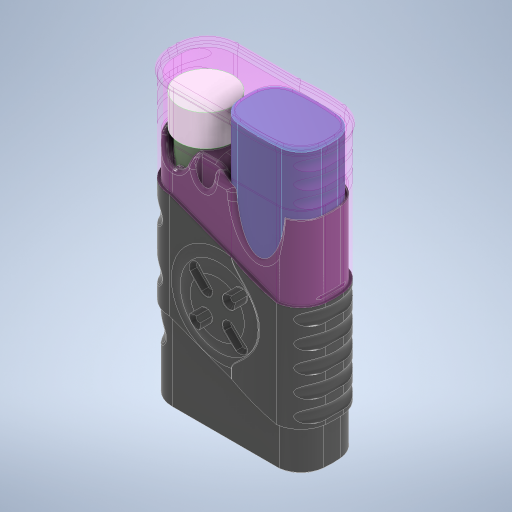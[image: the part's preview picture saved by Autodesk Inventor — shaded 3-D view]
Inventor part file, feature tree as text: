
AUTODESK INVENTOR PART (.ipt)
format: ipt  version: 2024.1 (Build 281209000, 209)  size: 4,207,616 bytes
history: native  units: mm
features: fillet x36, projected_geometry x32, extrude x28, sketch x14, other x6, revolve x6, sweep x2, pattern_circular x2, chamfer x2, plane x1, mirror x1
ambient origin geometry x8: Origin, YZ Plane, XZ Plane, XY Plane, X Axis, Y Axis, Z Axis, Center Point
bodies: Body1 (feature_tree), Body2 (feature_tree), Body3 (feature_tree), Body4 (feature_tree)
feature tree (130):
  other  "vape"
  extrude  "Extrusion1"  Depth=8.35mm
  fillet  "Fillet1"  Radius=80.0mm
  extrude  "Extrusion2"  Depth=11.6mm TaperAngle=0.0deg
  plane  "Work Plane1"
  extrude  "Extrusion3"  Depth=45.8mm TaperAngle=0.0deg
  extrude  "Extrusion4"  Depth=22.1mm
  extrude  "Extrusion5"  Depth=1.5mm
  extrude  "Extrusion6"  Depth=1.5mm
  fillet  "Fillet2"  Radius=1.5mm
  extrude  "Extrusion8"  Depth=15.55mm
  extrude  "Extrusion20"  Depth=3.0mm
  extrude  "Extrusion21"  Depth=3.0mm
  sweep  "Sweep2"
  extrude  "Extrusion22"  Depth=13.0mm
  fillet  "Fillet22"  Radius=2.0mm
  fillet  "Fillet23"  Radius=10.0mm
  fillet  "Fillet24"  Radius=11.0mm
  fillet  "Fillet25"  Radius=4.0mm
  fillet  "Fillet26"  Radius=2.0mm
  fillet  "Fillet4"  Radius=3.0mm
  extrude  "Extrusion10"  Depth=2.4mm
  extrude  "Extrusion11"  Depth=7.3mm
  fillet  "Fillet10"  Radius=7.0mm
  fillet  "Fillet27"  Radius=45.0mm
  extrude  "Extrusion13"  Depth=0.25mm
  fillet  "Fillet28"  Radius=71.0mm
  extrude  "Extrusion14"  Depth=71.0mm TaperAngle=0.0deg
  extrude  "Extrusion23"  Depth=3.0mm TaperAngle=30.0deg
  extrude  "Extrusion24"  Depth=1.0mm
  extrude  "Extrusion15"  Depth=15.0mm TaperAngle=0.0deg
  fillet  "Fillet29"  Radius=15.0mm
  extrude  "Extrusion25"  TaperAngle=0.0deg  [1 undecoded]
  fillet  "Fillet30"  [1 undecoded]
  other  "Work Axis1"
  sketch  "Sketch29"  dims[d28=17.0mm d29=45.8mm d30=0.0mm]
  revolve  "Revolution1"  [1 undecoded]
  sketch  "Sketch30"  dims[d31=17.0mm d38=22.1mm]
  revolve  "Revolution2"  [1 undecoded]
  fillet  "Fillet32"  Radius=20.0mm
  extrude  "Extrusion26"  Depth=9.0mm
  revolve  "Revolution3"  [1 undecoded]
  revolve  "Revolution5"  [1 undecoded]
  extrude  "Extrusion27"  Depth=4.0mm
  extrude  "Extrusion28"  Depth=1.0mm
  fillet  "Fillet34"  Radius=2.0mm
  other  "Work Axis2"
  revolve  "Revolution6"  [1 undecoded]
  pattern_circular  "Circular Pattern1"  [2 undecoded]
  extrude  "Extrusion29"  Depth=1.0mm
  fillet  "Fillet35"  Radius=24.0mm
  fillet  "Fillet36"  Radius=2.5mm
  fillet  "Fillet37"  Radius=0.7mm
  fillet  "Fillet38"  Radius=3.0mm
  fillet  "Fillet39"  Radius=5.0mm
  fillet  "Fillet40"  Radius=0.5mm
  fillet  "Fillet41"  Radius=10.0mm
  pattern_circular  "Circular Pattern2"  [2 undecoded]
  fillet  "Fillet42"  Radius=1.5mm
  fillet  "Fillet43"  Radius=6.0mm
  fillet  "Fillet44"  Radius=3.65mm
  fillet  "Fillet45"  Radius=10.0mm
  fillet  "Fillet46"  Radius=2.5mm
  extrude  "Extrusion30"  Depth=14.0mm
  extrude  "Extrusion36"  Depth=19.0mm
  chamfer  "Chamfer2"  Angle=180.0deg  [1 undecoded]
  mirror  "Mirror2"
  fillet  "Fillet51"  Radius=7.8mm
  fillet  "Fillet52"  Radius=8.0mm
  fillet  "Fillet53"  Radius=7.8mm
  fillet  "Fillet54"  Radius=7.8mm
  fillet  "Fillet55"  Radius=7.8mm
  fillet  "Fillet56"  [1 undecoded]
  extrude  "Extrusion31"  TaperAngle=180.0deg  [1 undecoded]
  extrude  "Extrusion32"  Depth=1.5mm
  sketch  "Sketch48"  dims[d48=3.0mm d49=3.0mm]
  sweep  "Sweep3"
  revolve  "Revolution8"  [1 undecoded]
  fillet  "Fillet48"  Radius=6.0mm
  chamfer  "Chamfer3"  Distance=6.0mm
  extrude  "Extrusion33"  Depth=11.5mm
  extrude  "Extrusion34"  Depth=6.0mm
  fillet  "Fillet49"  Radius=6.0mm
  fillet  "Fillet50"  [1 undecoded]
  other  "vape-tube"
  other  "storage"
  projected_geometry  "Projected Loop2"
  projected_geometry  "Projected Loop3"
  projected_geometry  "Projected Loop4"
  projected_geometry  "Projected Loop6"
  other  "vape-lid"
  projected_geometry  "Projected Loop13"
  sketch  "Sketch23"  dims[d4=98.5mm d5=0.0mm d9=8.35mm d22=80.0mm d23=0.0mm]
  projected_geometry  "Projected Loop14"
  sketch  "Sketch25"  dims[d24=20.0mm d26=11.6mm d27=0.0mm]
  projected_geometry  "Projected Loop15"
  projected_geometry  "Projected Loop16"
  projected_geometry  "Projected Loop17"
  projected_geometry  "Projected Loop18"
  projected_geometry  "Projected Loop19"
  projected_geometry  "Projected Loop20"
  projected_geometry  "Projected Loop31"
  sketch  "Sketch37"  dims[d39=31.1mm d41=1.5mm]
  projected_geometry  "Projected Loop32"
  projected_geometry  "Projected Loop33"
  projected_geometry  "Projected Loop34"
  projected_geometry  "Projected Loop35"
  sketch  "Sketch45"  dims[d42=1.5mm d44=1.5mm d45=1.5mm]
  projected_geometry  "Projected Loop36"
  projected_geometry  "Projected Loop37"
  projected_geometry  "Projected Loop38"
  projected_geometry  "Projected Loop39"
  sketch  "Sketch47"  dims[d46=11.05mm d47=15.55mm]
  sketch  "Sketch49"  dims[d50=3.0mm d51=3.0mm]
  projected_geometry  "Projected Loop46"
  projected_geometry  "Projected Loop47"
  sketch  "3D Sketch1"
  projected_geometry  "Projected Loop48"
  projected_geometry  "Projected Loop49"
  projected_geometry  "Projected Loop50"
  projected_geometry  "Projected Loop51"
  sketch  "Sketch51"  dims[d52=11.05mm d53=15.55mm]
  sketch  "Sketch52"  dims[d54=2.0mm d55=13.0mm]
  projected_geometry  "Projected Loop53"
  sketch  "Sketch53"  dims[d56=12.5mm d57=60.0mm d58=0.0mm d59=2.0mm d60=10.0mm d61=0.0mm d62=11.0mm d66=4.0mm d67=0.0mm d69=2.0mm d83=3.0mm]
  sketch  "Sketch55"  dims[d86=72.0mm d87=0.0mm d88=2.4mm d89=7.3mm d91=7.0mm d92=45.0mm d93=0.0mm d94=0.25mm d105=71.0mm d106=0.0mm d108=71.0mm d109=0.0mm d110=3.0mm d111=30.0deg d158=1.0mm d159=15.0mm d160=0.0mm d161=15.0mm d162=0.0mm d163=0.0mm d164=0.0mm d169=0.0mm d170=0.0mm d171=15.0mm d172=15.780931mm d173=20.0mm d174=9.0mm d175=7.5mm d176=6.0mm d177=4.0mm d178=1.0mm d179=2.0mm d180=1.2mm d181=0.5mm d182=1.0mm d183=24.0mm d184=2.5mm d185=0.7mm d186=3.0mm d187=5.0mm d188=0.5mm d189=10.0mm d190=0.0mm d191=10.0mm d192=0.0mm d193=1.5mm d194=6.0mm d195=3.65mm d196=10.0mm d197=0.0mm d198=2.5mm d199=14.0mm d200=19.0mm d201=19.0mm d207=180.0deg d208=7.8mm d209=8.0mm d210=7.8mm d211=7.8mm d212=7.8mm d215=0.0mm d216=180.0deg d218=1.5mm d220=0.5mm d221=18.25mm d222=0.0mm d225=6.0mm d226=6.0mm d227=11.5mm d228=6.0mm d229=6.0mm d230=180.0deg d240=3.0mm d241=6.0mm d242=6.0mm d243=6.0mm d244=41.5mm d245=11.5mm d246=6.0mm d247=180.0deg d249=20.0mm d253=22.0mm d254=22.0mm d255=25.0mm d256=1.0mm d257=1.0mm d258=0.0mm d259=1.0mm d260=0.0mm d261=0.2mm d263=5.0mm d264=10.0mm d265=2.241222mm d266=10.0mm d267=30.0mm d268=4.0mm d269=45.0deg d270=40.0mm d271=360.0deg d275=0.4mm d276=1.1mm d277=2.4mm d278=3.0mm d279=1.5mm d280=3.0mm d281=0.810487mm d282=2.943591mm d283=4.5mm d284=0.0mm d285=2.0mm d286=0.8mm d287=3.0mm d288=0.5mm d289=1.0mm d290=1.0mm d291=1.0mm d292=40.0mm d293=360.0deg d295=1.0mm d296=0.5mm d297=0.5mm d298=1.0mm d299=0.4mm d312=12.0mm d315=8.5mm d316=8.5mm d317=5.0mm d318=40.0mm d320=360.0deg d322=10.0mm d323=0.5mm d324=0.0mm d325=0.0mm d329=1.5mm d330=2.0mm d331=45.0deg d332=21.0mm d334=5.458726mm d335=19.0mm d336=30.0mm d337=42.5mm d338=30.0mm d339=0.0mm d340=15.0mm d341=0.0mm d342=0.0mm d343=0.0mm d344=29.760104mm d349=22.0mm d350=24.0mm d351=180.0deg d352=2.0mm d353=0.5mm d354=15.0mm d355=45.0deg d365=1.5mm d366=1.5mm d367=15.0mm d368=0.0mm d369=1.5mm d370=0.25mm d371=0.25mm d372=1.4mm d373=1.5mm d374=1.5mm d375=7.5mm d376=0.0mm d377=0.4mm d378=0.4mm d385=32.0mm d386=1.25mm d387=0.0mm d388=16.0mm d389=15.0mm d390=2.0mm d391=15.0mm d392=13.0mm d393=1.0mm]
  projected_geometry  "Projected Loop54"
  projected_geometry  "Projected Loop55"
  projected_geometry  "Projected Loop56"
  projected_geometry  "Projected Loop57"
note: 16 required parameter values undecoded (feature->parameter linkage not recoverable at this tier; creation-order binding heuristic only, values carry confidence <= 0.55)